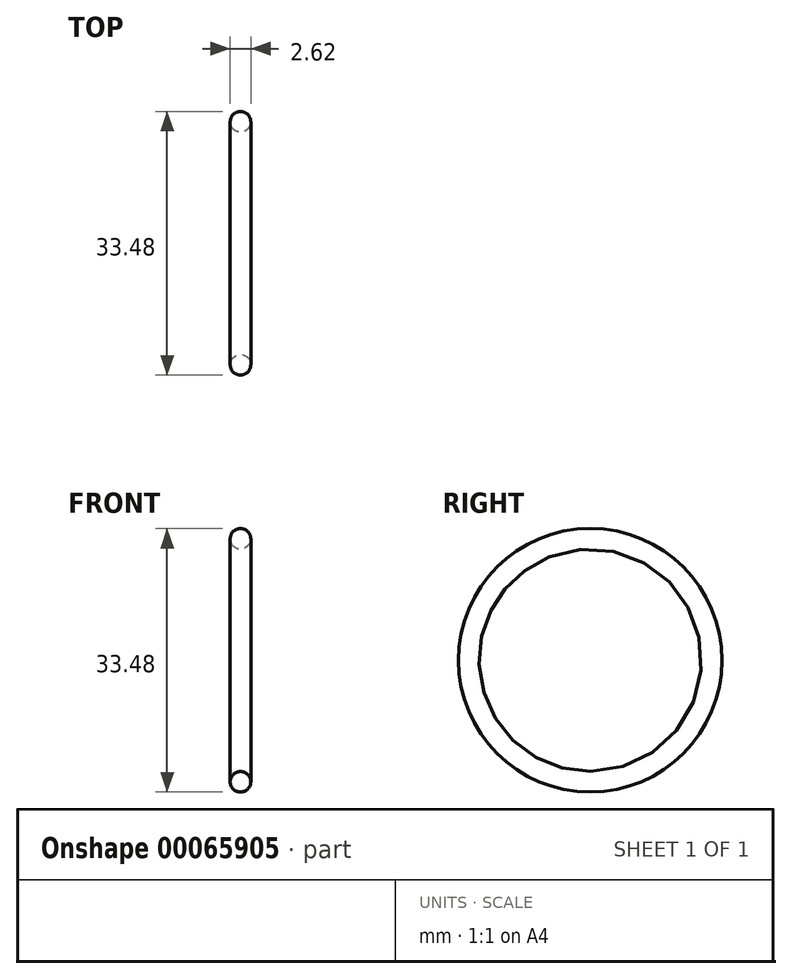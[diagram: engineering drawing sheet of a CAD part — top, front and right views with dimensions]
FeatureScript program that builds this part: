
annotation { "Feature Type Name" : "Feature", "Feature Type Description" : "" }
export const myFeature = defineFeature(function(context is Context, id is Id, definition is map)
    precondition{}
    {
        {
            var Q0;
            Q0=qCreatedBy(makeId("Front.planeOp"),FACE);
            var sketch = newSketch(context, id + "F0", { "sketchPlane" : qUnion([Q0])});
            skLineSegment(sketch, "E0", {"start": v(0, 0) * mm, "end": v(-6.06, 0) * mm, "construction": true});
            skCircle(sketch, "E1", {"center": v(0, 15.43) * mm, "radius": 1.3 * mm});
            skSolve(sketch);
        }
        {
            var Q0;
            Q0=makeQuery(id+"F0.imprint","IMPRINT",FACE,{"disambiguationData":[TD([[makeQuery(id+"F0.imprint","IMPRINT",EDGE,{"derivedFrom":sQuery(id+"F0.wireOp",EDGE,"E1")}),1.0]])]});
            var Q1;
            Q1=sQuery(id+"F0.wireOp",EDGE,"E0");
            revolve(context, id + "F1", {"entities" : qUnion([Q0]), "axis" : qUnion([Q1]), "revolveType" : RevolveType.FULL});
        }
    });
